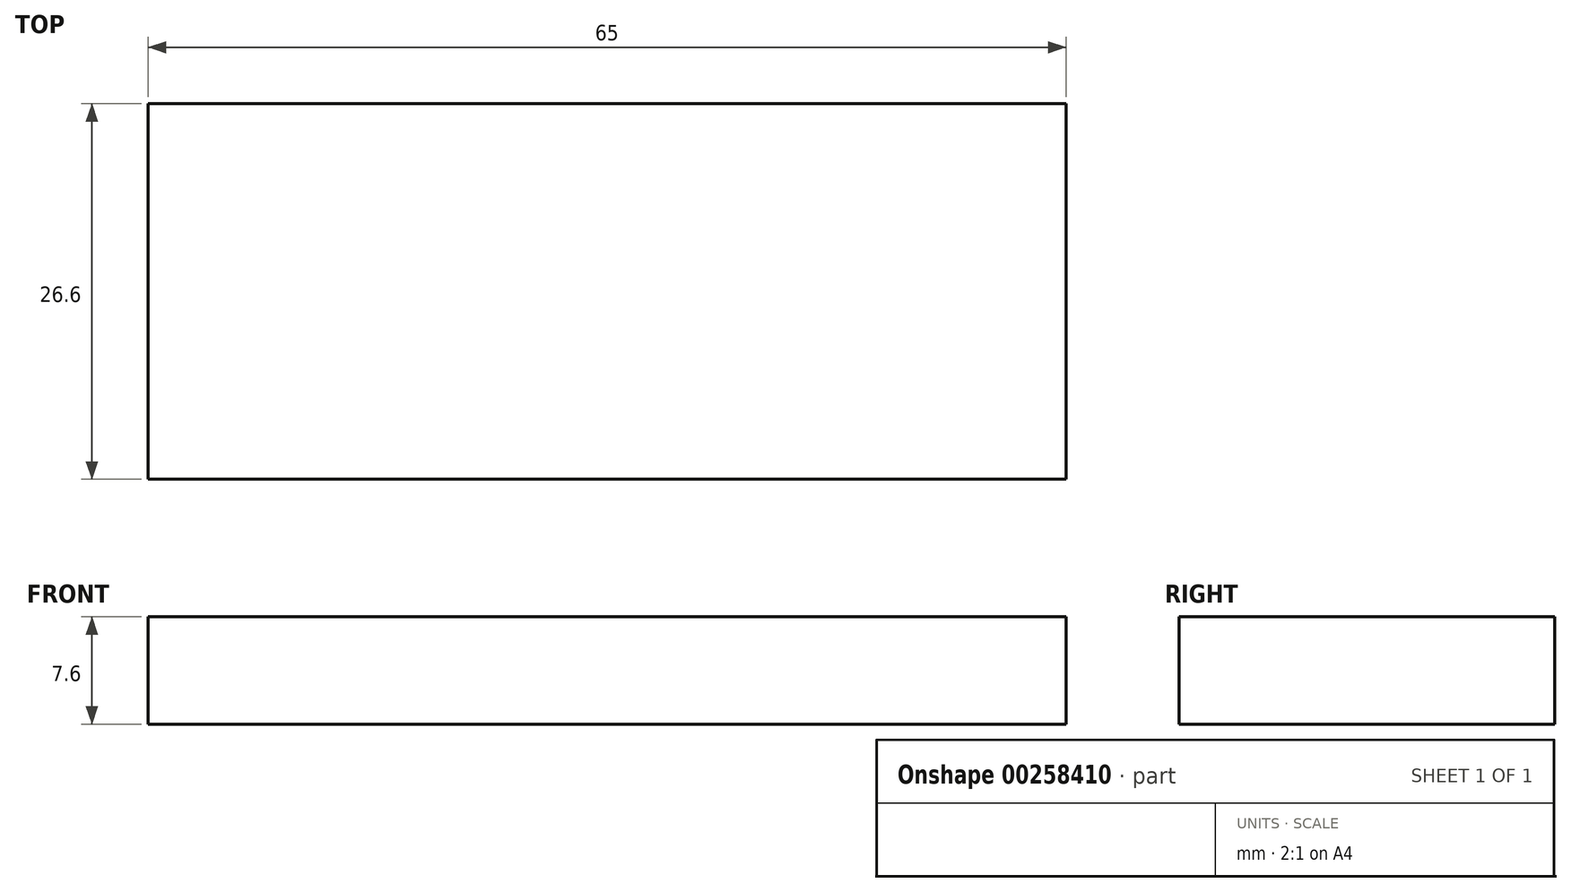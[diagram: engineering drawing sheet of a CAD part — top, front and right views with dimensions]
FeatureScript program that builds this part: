
annotation { "Feature Type Name" : "Feature", "Feature Type Description" : "" }
export const myFeature = defineFeature(function(context is Context, id is Id, definition is map)
    precondition{}
    {
        {
            var Q0;
            Q0=qCreatedBy(makeId("Top.planeOp"),FACE);
            var sketch = newSketch(context, id + "F0", { "sketchPlane" : qUnion([Q0])});
            skLineSegment(sketch, "E0.bottom", {"start": v(32.5, -13.3) * mm, "end": v(-32.5, -13.3) * mm});
            skLineSegment(sketch, "E0.top", {"start": v(32.5, 13.3) * mm, "end": v(-32.5, 13.3) * mm});
            skLineSegment(sketch, "E0.left", {"start": v(32.5, -13.3) * mm, "end": v(32.5, 13.3) * mm});
            skLineSegment(sketch, "E0.right", {"start": v(-32.5, -13.3) * mm, "end": v(-32.5, 13.3) * mm});
            skPoint(sketch, "E0.middle", {"position": v(0, 0) * mm});
            skSolve(sketch);
        }
        {
            var Q0;
            Q0=makeQuery(id+"F0.imprint","IMPRINT",FACE,{"disambiguationData":[TD([[makeQuery(id+"F0.imprint","IMPRINT",EDGE,{"derivedFrom":sQuery(id+"F0.wireOp",EDGE,"E0.bottom")}),-1.0]])]});
            extrude(context, id + "F1", {"entities" : qUnion([Q0]), "depth" : 3.8 * mm, "hasSecondDirection" : true, "secondDirectionOppositeDirection" : true, "secondDirectionDepth" : 3.8 * mm});
        }
    });
